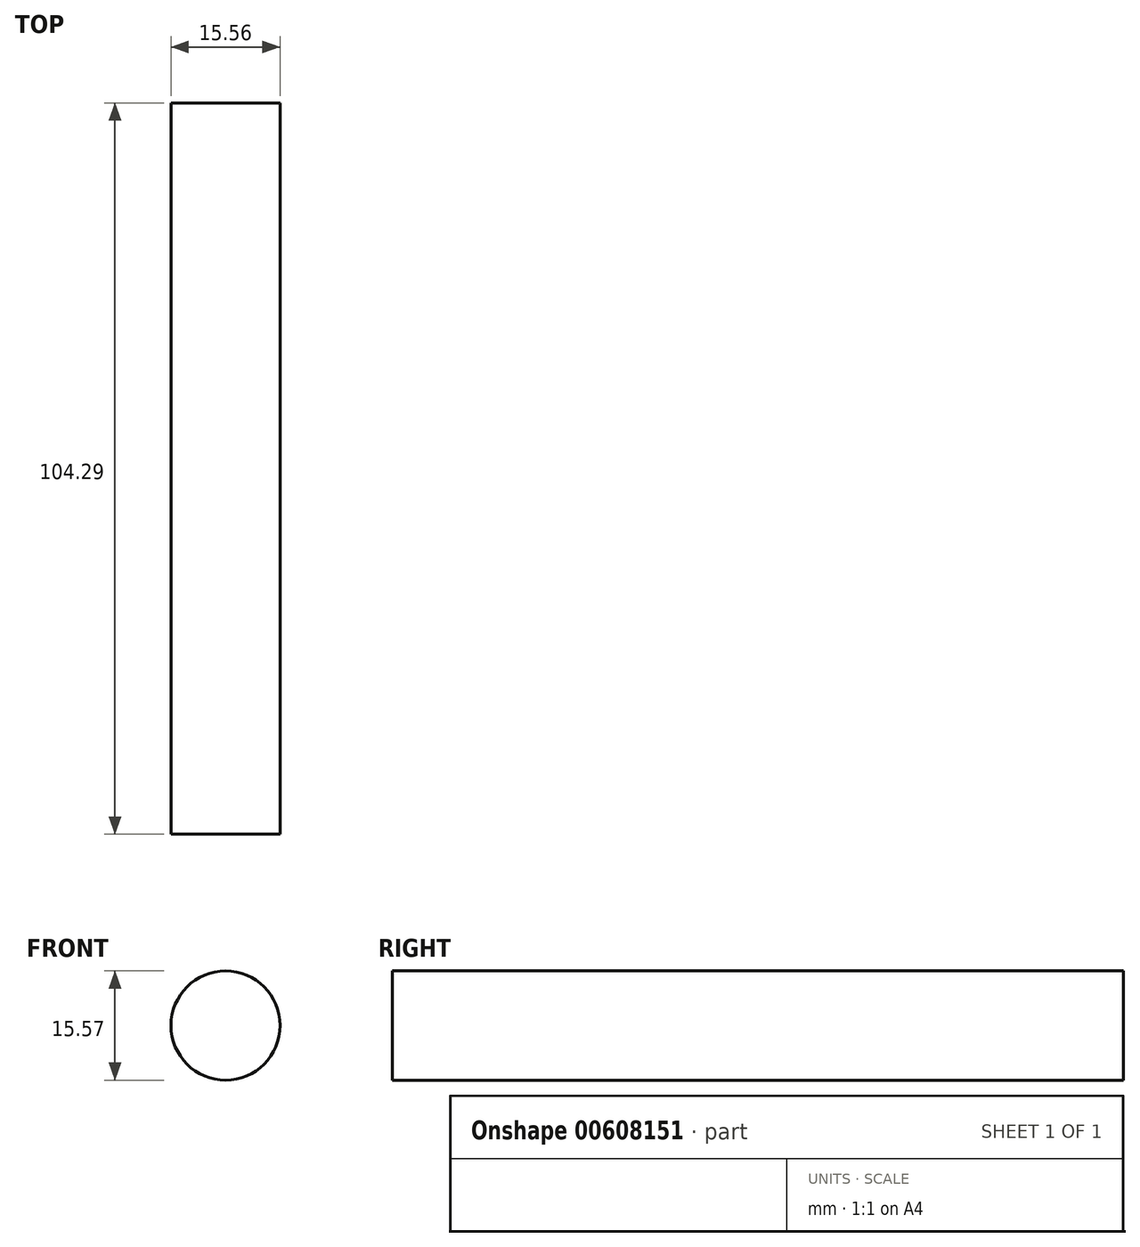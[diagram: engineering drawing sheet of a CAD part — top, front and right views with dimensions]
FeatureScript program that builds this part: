
annotation { "Feature Type Name" : "Feature", "Feature Type Description" : "" }
export const myFeature = defineFeature(function(context is Context, id is Id, definition is map)
    precondition{}
    {
        {
            var Q0;
            Q0=qCreatedBy(makeId("Front.planeOp"),FACE);
            var sketch = newSketch(context, id + "F0", { "sketchPlane" : qUnion([Q0])});
            skCircle(sketch, "E0", {"center": v(-60.43, 37.15) * mm, "radius": 7.78 * mm});
            skSolve(sketch);
        }
        {
            var Q0;
            Q0 = qSketchRegion(id + "F0", true);
            extrude(context, id + "F1", {"entities" : qUnion([Q0]), "depth" : 104.3 * mm, "offsetDistance" : 25.4 * mm});
        }
    });
